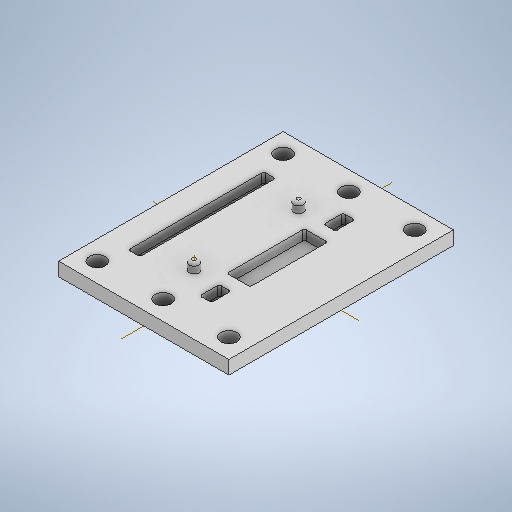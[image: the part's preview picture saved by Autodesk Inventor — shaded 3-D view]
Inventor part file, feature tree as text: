
AUTODESK INVENTOR PART (.ipt)
format: ipt  version: 2025 (Build 290162000, 162)  size: 329,728 bytes
history: native  units: mm
features: sketch x6, extrude x5, mirror x2, fillet x2, hole x1, pattern_linear x1, other x1
ambient origin geometry x8: Origin, YZ Plane, XZ Plane, XY Plane, X Axis, Y Axis, Z Axis, Center Point
bodies: Solid1 (feature_tree)
feature tree (18):
  extrude  "Extrusion1"  Depth=58.0mm
  hole  "Hole1"  [1 undecoded]
  pattern_linear  "Rectangular Pattern1"  Count1=2 Spacing1=17.0mm
  mirror  "Mirror1"
  extrude  "Extrusion2"  Depth=2.5mm
  fillet  "Fillet1"  Radius=2.5mm
  extrude  "Extrusion3"  Depth=2.5mm TaperAngle=0.0deg
  other  "Work Axis1"
  extrude  "Extrusion4"  Depth=2.5mm
  extrude  "Extrusion5"  Depth=3.0mm
  mirror  "Mirror2"
  fillet  "Fillet2"  Radius=35.0mm
  sketch  "Sketch1"  dims[d2=44.0mm d3=58.0mm]
  sketch  "Sketch2"  dims[d13=3.5mm d14=0.0mm]
  sketch  "Sketch3"  dims[d15=4.2mm d16=6.0mm d17=4.0mm d18=2.0mm d19=90.0deg d20=8.0mm d21=20.594885mm d22=5.0mm d23=20.0mm d25=17.0mm]
  sketch  "Sketch4"  dims[d26=20.0mm d28=17.0mm d29=2.5mm d30=2.5mm]
  sketch  "Sketch5"  dims[d31=13.5mm d32=2.5mm d33=0.0mm]
  sketch  "Sketch6"  dims[d34=0.75mm d35=2.5mm d36=3.0mm d37=35.0mm d38=0.0mm d39=14.0mm d40=6.0mm d41=2.5mm d42=8.0mm d43=20.0mm d44=0.0mm d45=3.0mm d46=5.0mm d47=3.0mm d48=3.5mm d49=2.5mm d50=0.0mm d51=0.5mm]
note: 1 required parameter value undecoded (feature->parameter linkage not recoverable at this tier; creation-order binding heuristic only, values carry confidence <= 0.55)
